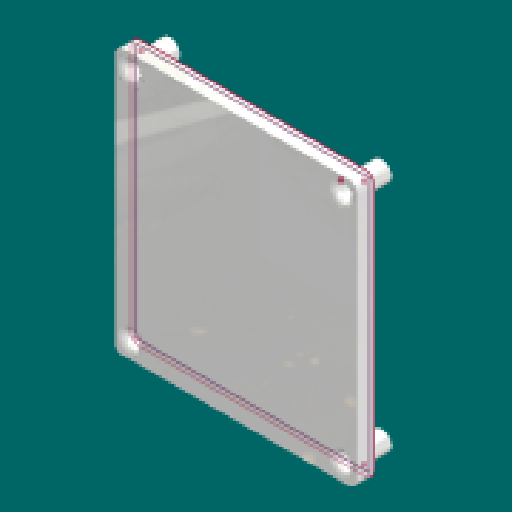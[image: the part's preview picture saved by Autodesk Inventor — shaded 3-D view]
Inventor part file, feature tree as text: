
AUTODESK INVENTOR PART (.ipt)
format: ipt  version: 2025.2 (Build 292293000, 293)  size: 476,672 bytes
history: native  units: mm
features: reference x24, sketch x15, extrude x14, projected_geometry x10, fillet x5, other x3, plane x2
ambient origin geometry x8: Origin, YZ Plane, XZ Plane, XY Plane, X Axis, Y Axis, Z Axis, Center Point
bodies: Solid1 (feature_tree)
feature tree (73):
  plane  "Work Plane1"
  sketch  "Sketch1"  dims[d0=5.0mm d2=90.0mm]
  plane  "Work Plane2"
  sketch  "Sketch2"  dims[d3=80.0mm d4=5.0mm d5=0.0mm]
  extrude  "Extrusion1"  Depth=90.0mm
  extrude  "Extrusion2"  Depth=5.0mm TaperAngle=0.0deg
  extrude  "Extrusion3"  Depth=3.0mm TaperAngle=0.0deg
  fillet  "Fillet1"  Radius=0.3mm
  extrude  "Extrusion4"  Depth=0.3mm
  extrude  "Extrusion5"  Depth=3.0mm TaperAngle=0.0deg
  extrude  "Extrusion6"  Depth=1.5mm
  extrude  "Extrusion7"  Depth=3.0mm TaperAngle=0.0deg
  extrude  "Extrusion8"  Depth=5.0mm
  fillet  "Fillet3"  Radius=5.0mm
  fillet  "Fillet4"  Radius=6.7mm
  extrude  "Extrusion9"  Depth=3.2mm
  extrude  "Extrusion10"  Depth=3.2mm
  extrude  "Extrusion11"  Depth=10.0mm TaperAngle=0.0deg
  extrude  "Extrusion12"  Depth=1.0mm
  fillet  "Fillet5"  Radius=1.0mm
  fillet  "Fillet6"  Radius=1.0mm
  extrude  "Extrusion13"  Depth=10.0mm
  extrude  "Extrusion14"  Depth=8.2mm
  reference  "Reference1"
  reference  "Reference2"
  reference  "Reference3"
  reference  "Reference4"
  reference  "Reference5"
  reference  "Reference6"
  reference  "Reference7"
  reference  "Reference8"
  reference  "Reference9"
  reference  "Reference10"
  reference  "Reference11"
  reference  "Reference12"
  sketch  "Sketch3"  dims[d6=0.3mm d7=3.0mm d8=0.0mm d9=0.3mm]
  reference  "Reference13"
  reference  "Reference14"
  reference  "Reference15"
  reference  "Reference16"
  reference  "Reference17"
  reference  "Reference18"
  reference  "Reference19"
  reference  "Reference20"
  reference  "Reference21"
  reference  "Reference22"
  reference  "Reference23"
  reference  "Reference24"
  sketch  "Sketch4"  dims[d10=0.3mm d11=0.3mm]
  projected_geometry  "Projected Loop1"
  sketch  "Sketch5"  dims[d12=0.3mm d13=3.0mm d14=0.0mm]
  sketch  "Sketch6"  dims[d15=1.0mm d16=1.5mm]
  sketch  "Sketch7"  dims[d17=1.5mm d18=3.0mm d19=0.0mm]
  sketch  "Sketch8"  dims[d21=5.0mm d22=0.0mm d23=5.0mm d24=5.0mm d25=0.0mm d30=6.7mm]
  sketch  "Sketch9"  dims[d31=6.0mm d32=3.2mm]
  projected_geometry  "Projected Loop2"
  projected_geometry  "Projected Loop3"
  projected_geometry  "Projected Loop4"
  sketch  "Sketch10"  dims[d33=46.0mm d34=3.2mm]
  projected_geometry  "Projected Loop5"
  sketch  "Sketch11"  dims[d35=3.2mm d36=10.0mm d37=0.0mm]
  projected_geometry  "Projected Loop6"
  sketch  "Sketch12"  dims[d38=1.0mm d39=1.0mm d40=1.0mm d41=1.0mm]
  projected_geometry  "Projected Loop7"
  projected_geometry  "Projected Loop8"
  sketch  "Sketch13"  dims[d42=10.0mm d43=0.0mm d44=2.0mm]
  projected_geometry  "Projected Loop9"
  sketch  "Sketch14"  dims[d45=1.0mm d46=8.2mm]
  projected_geometry  "Projected Loop10"
  sketch  "Sketch15"  dims[d47=10.0mm d48=0.0mm d49=1.5mm d50=10.0mm d51=0.0mm d52=35.17mm d53=10.0mm d54=0.0mm d55=10.0mm d56=0.0mm d57=2.0mm d58=1.0mm d59=2.0mm d60=3.0mm d61=3.0mm d62=5.0mm d63=0.0mm d64=3.0mm d65=10.0mm d66=0.0mm]
  other  "<userpath>\OneDrive\Dokumen\fiqhin\Ass_fiqh.iam"
  other  "Ass_fiqh.iam"
  other  "arduino uno:1"
